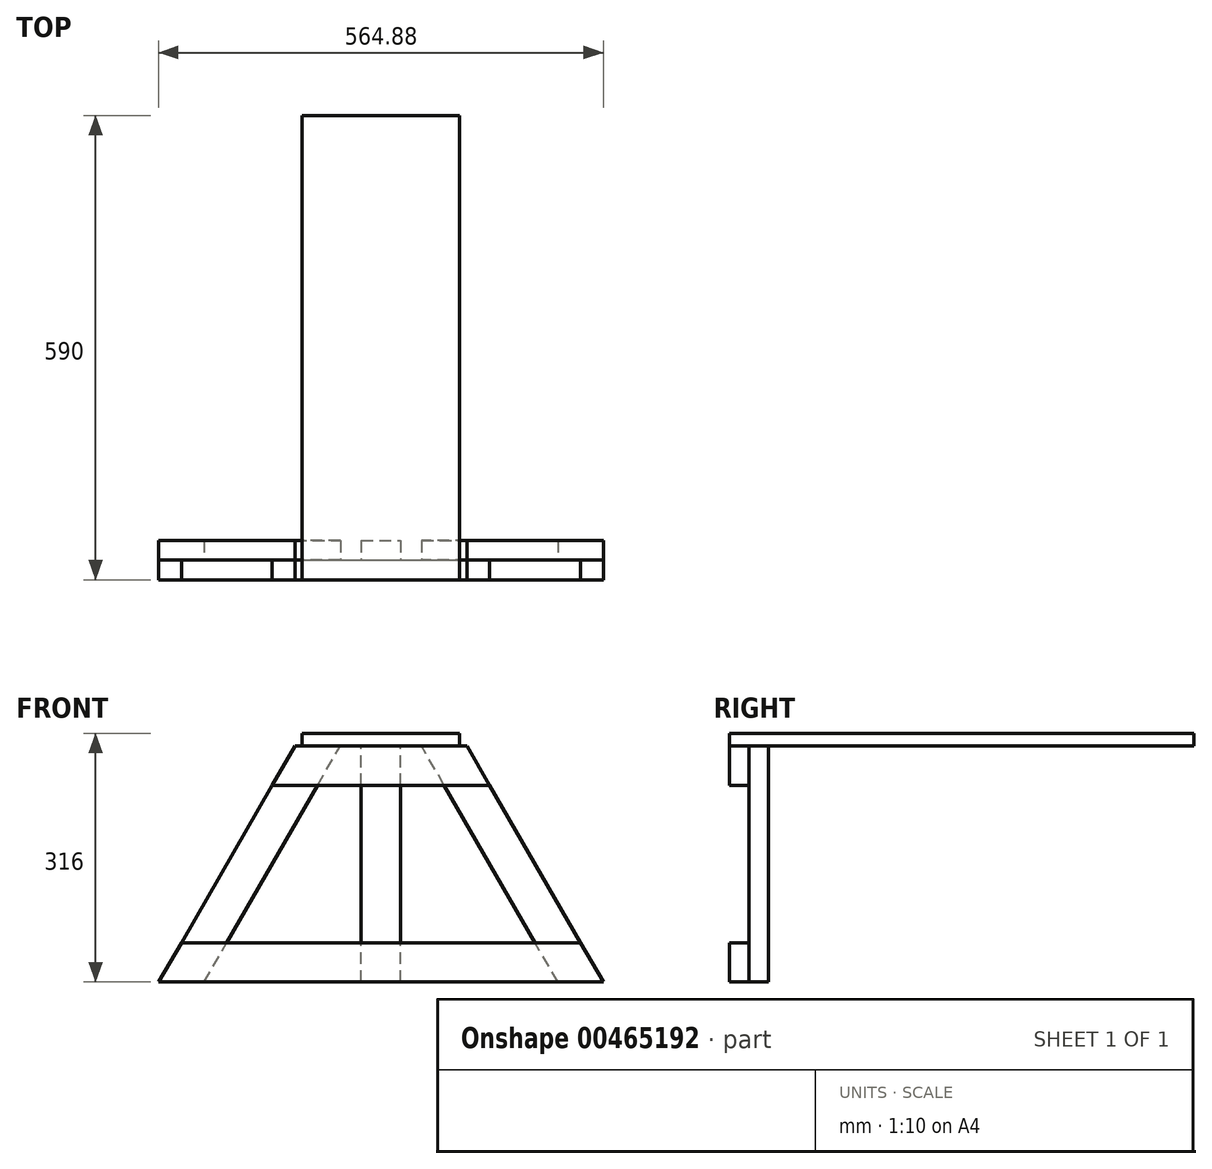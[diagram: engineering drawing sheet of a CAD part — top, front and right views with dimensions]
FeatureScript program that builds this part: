
annotation { "Feature Type Name" : "Feature", "Feature Type Description" : "" }
export const myFeature = defineFeature(function(context is Context, id is Id, definition is map)
    precondition{}
    {
        {
            var Q0;
            Q0=qCreatedBy(makeId("Front.planeOp"),FACE);
            var sketch = newSketch(context, id + "F0", { "sketchPlane" : qUnion([Q0])});
            skLineSegment(sketch, "E0.bottom", {"start": v(-100, 300) * mm, "end": v(100, 300) * mm});
            skLineSegment(sketch, "E0.top", {"start": v(-100, 316) * mm, "end": v(100, 316) * mm});
            skLineSegment(sketch, "E0.left", {"start": v(-100, 300) * mm, "end": v(-100, 316) * mm});
            skLineSegment(sketch, "E0.right", {"start": v(100, 300) * mm, "end": v(100, 316) * mm});
            skSolve(sketch);
        }
        {
            var Q0;
            Q0=makeQuery(id+"F0.imprint","IMPRINT",FACE,{"disambiguationData":[TD([[makeQuery(id+"F0.imprint","IMPRINT",EDGE,{"derivedFrom":sQuery(id+"F0.wireOp",EDGE,"E0.bottom")}),1.0]])]});
            extrude(context, id + "F1", {"entities" : qUnion([Q0]), "oppositeDirection" : true, "depth" : 590 * mm});
        }
        {
            var Q0;
            Q0=qCreatedBy(makeId("Front.planeOp"),FACE);
            var sketch = newSketch(context, id + "F2", { "sketchPlane" : qUnion([Q0])});
            skLineSegment(sketch, "E1.bottom", {"start": v(-138.1, 250) * mm, "end": v(138.1, 250) * mm});
            skLineSegment(sketch, "E1.top", {"start": v(-109.24, 300) * mm, "end": v(109.24, 300) * mm});
            skLineSegment(sketch, "E1.left", {"start": v(-138.1, 250) * mm, "end": v(-109.24, 300) * mm});
            skLineSegment(sketch, "E1.right", {"start": v(138.1, 250) * mm, "end": v(109.24, 300) * mm});
            skSolve(sketch);
        }
        {
            var Q0;
            Q0=makeQuery(id+"F2.imprint","IMPRINT",FACE,{"disambiguationData":[TD([[makeQuery(id+"F2.imprint","IMPRINT",EDGE,{"derivedFrom":sQuery(id+"F2.wireOp",EDGE,"E1.bottom")}),1.0]])]});
            extrude(context, id + "F3", {"entities" : qUnion([Q0]), "oppositeDirection" : true, "depth" : 25 * mm});
        }
        {
            var Q0;
            Q0=qCreatedBy(makeId("Front.planeOp"),FACE);
            var sketch = newSketch(context, id + "F4", { "sketchPlane" : qUnion([Q0])});
            skLineSegment(sketch, "E2.bottom", {"start": v(-282.44, 0) * mm, "end": v(282.44, 0) * mm});
            skLineSegment(sketch, "E2.top", {"start": v(-253.58, 50) * mm, "end": v(253.58, 50) * mm});
            skLineSegment(sketch, "E2.left", {"start": v(-282.44, 0) * mm, "end": v(-253.58, 50) * mm});
            skLineSegment(sketch, "E2.right", {"start": v(282.44, 0) * mm, "end": v(253.58, 50) * mm});
            skSolve(sketch);
        }
        {
            var Q0;
            Q0=makeQuery(id+"F4.imprint","IMPRINT",FACE,{"disambiguationData":[TD([[makeQuery(id+"F4.imprint","IMPRINT",EDGE,{"derivedFrom":sQuery(id+"F4.wireOp",EDGE,"E2.bottom")}),1.0]])]});
            extrude(context, id + "F5", {"entities" : qUnion([Q0]), "oppositeDirection" : true, "depth" : 25 * mm});
        }
        {
            var Q0;
            Q0=makeQuery(id+"F3.opExtrude","CAP_FACE",FACE,{"disambiguationData":[OSD([sQuery(id+"F2.wireOp",EDGE,"E1.bottom"),sQuery(id+"F2.wireOp",EDGE,"E1.top"),sQuery(id+"F2.wireOp",EDGE,"E1.left"),sQuery(id+"F2.wireOp",EDGE,"E1.right")])],"isStart":false});
            var sketch = newSketch(context, id + "F6", { "sketchPlane" : qUnion([Q0])});
            skLineSegment(sketch, "E3.bottom", {"start": v(25, 0) * mm, "end": v(-25, 0) * mm});
            skLineSegment(sketch, "E3.top", {"start": v(25, 300) * mm, "end": v(-25, 300) * mm});
            skLineSegment(sketch, "E3.left", {"start": v(25, 0) * mm, "end": v(25, 300) * mm});
            skLineSegment(sketch, "E3.right", {"start": v(-25, 0) * mm, "end": v(-25, 300) * mm});
            skSolve(sketch);
        }
        {
            var Q0;
            Q0 = qSketchRegion(id + "F6", true);
            extrude(context, id + "F7", {"entities" : qUnion([Q0]), "depth" : 25 * mm});
        }
        {
            var Q0;
            Q0=makeQuery(id+"F3.opExtrude","CAP_FACE",FACE,{"disambiguationData":[OSD([sQuery(id+"F2.wireOp",EDGE,"E1.bottom"),sQuery(id+"F2.wireOp",EDGE,"E1.top"),sQuery(id+"F2.wireOp",EDGE,"E1.left"),sQuery(id+"F2.wireOp",EDGE,"E1.right")])],"isStart":false});
            var sketch = newSketch(context, id + "F8", { "sketchPlane" : qUnion([Q0])});
            skLineSegment(sketch, "E4.bottom", {"start": v(-282.44, 0) * mm, "end": v(-224.7, 0) * mm});
            skLineSegment(sketch, "E4.top", {"start": v(-109.24, 300) * mm, "end": v(-51.5, 300) * mm});
            skLineSegment(sketch, "E4.left", {"start": v(-282.44, 0) * mm, "end": v(-109.24, 300) * mm});
            skLineSegment(sketch, "E4.right", {"start": v(-224.7, 0) * mm, "end": v(-51.5, 300) * mm});
            skSolve(sketch);
        }
        {
            var Q0;
            Q0 = qSketchRegion(id + "F8", true);
            extrude(context, id + "F9", {"entities" : qUnion([Q0]), "depth" : 25 * mm});
        }
        {
            var Q0;
            Q0=makeQuery(id+"F9.opExtrude","SWEPT_BODY",BODY,{"disambiguationData":[OSD([sQuery(id+"F8.wireOp",EDGE,"E4.bottom"),sQuery(id+"F8.wireOp",EDGE,"E4.top"),sQuery(id+"F8.wireOp",EDGE,"E4.left"),sQuery(id+"F8.wireOp",EDGE,"E4.right")])]});
            var Q1;
            Q1=qCreatedBy(makeId("Right.planeOp"),FACE);
            mirror(context, id + "F10", {"entities" : qUnion([Q0]), "mirrorPlane" : qUnion([Q1])});
        }
    });
